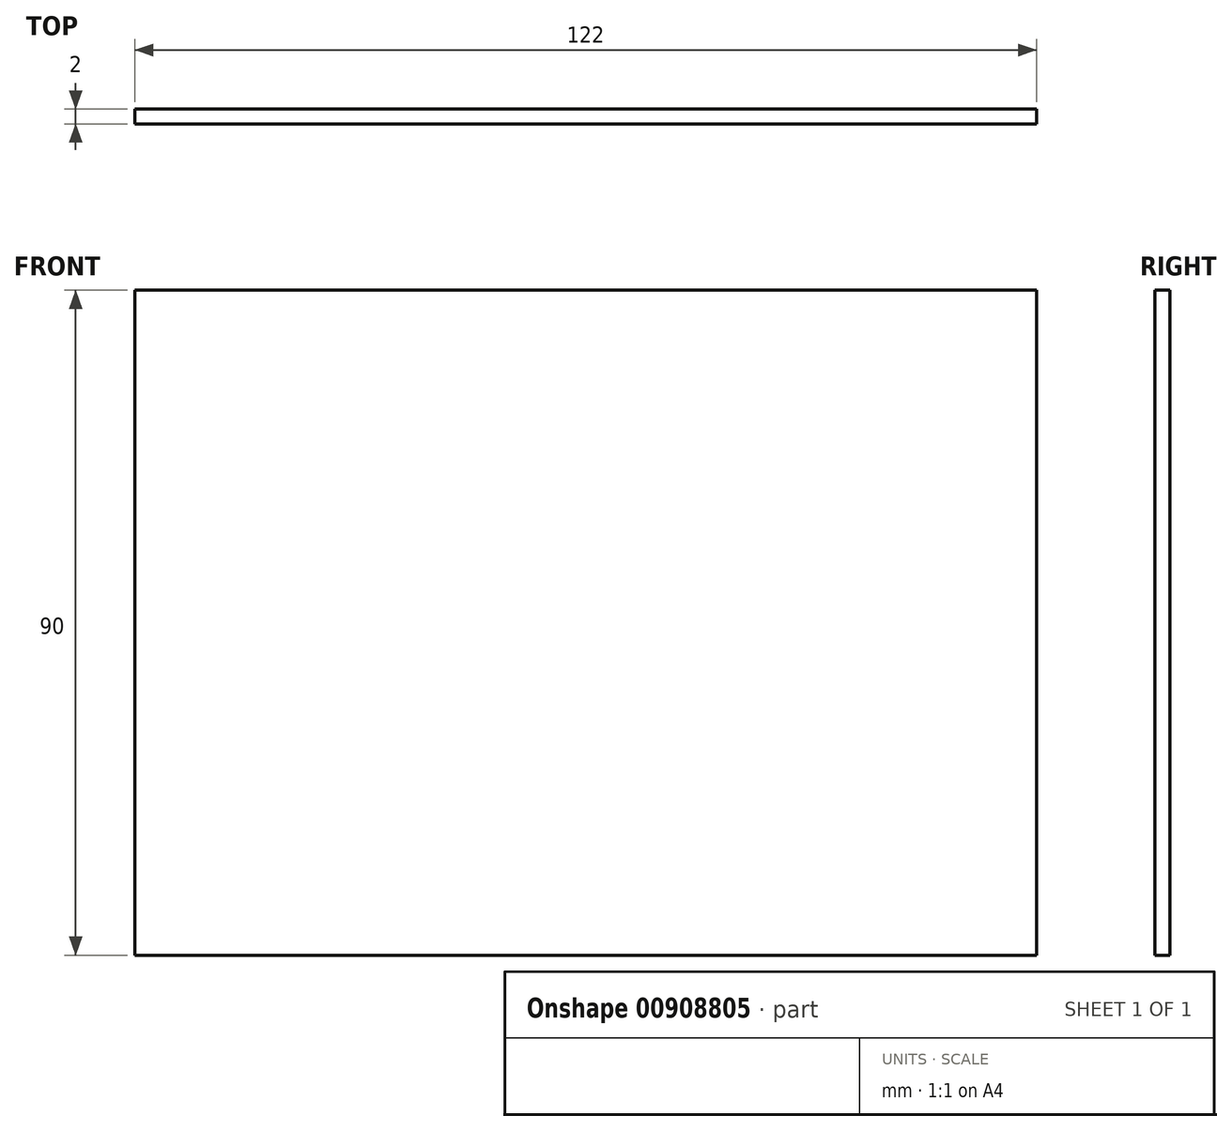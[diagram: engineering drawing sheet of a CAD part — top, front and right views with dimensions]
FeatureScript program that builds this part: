
annotation { "Feature Type Name" : "Feature", "Feature Type Description" : "" }
export const myFeature = defineFeature(function(context is Context, id is Id, definition is map)
    precondition{}
    {
        {
            var Q0;
            Q0=qCreatedBy(makeId("Front.planeOp"),FACE);
            var sketch = newSketch(context, id + "F0", { "sketchPlane" : qUnion([Q0])});
            skLineSegment(sketch, "E0.bottom", {"start": v(61, -45) * mm, "end": v(-61, -45) * mm});
            skLineSegment(sketch, "E0.top", {"start": v(61, 45) * mm, "end": v(-61, 45) * mm});
            skLineSegment(sketch, "E0.left", {"start": v(61, -45) * mm, "end": v(61, 45) * mm});
            skLineSegment(sketch, "E0.right", {"start": v(-61, -45) * mm, "end": v(-61, 45) * mm});
            skPoint(sketch, "E0.middle", {"position": v(0, 0) * mm});
            skSolve(sketch);
        }
        {
            var Q0;
            Q0=qSketchRegion(id+"F0",true);
            extrude(context, id + "F1", {"entities" : qUnion([Q0]), "depth" : 2 * mm});
        }
    });
